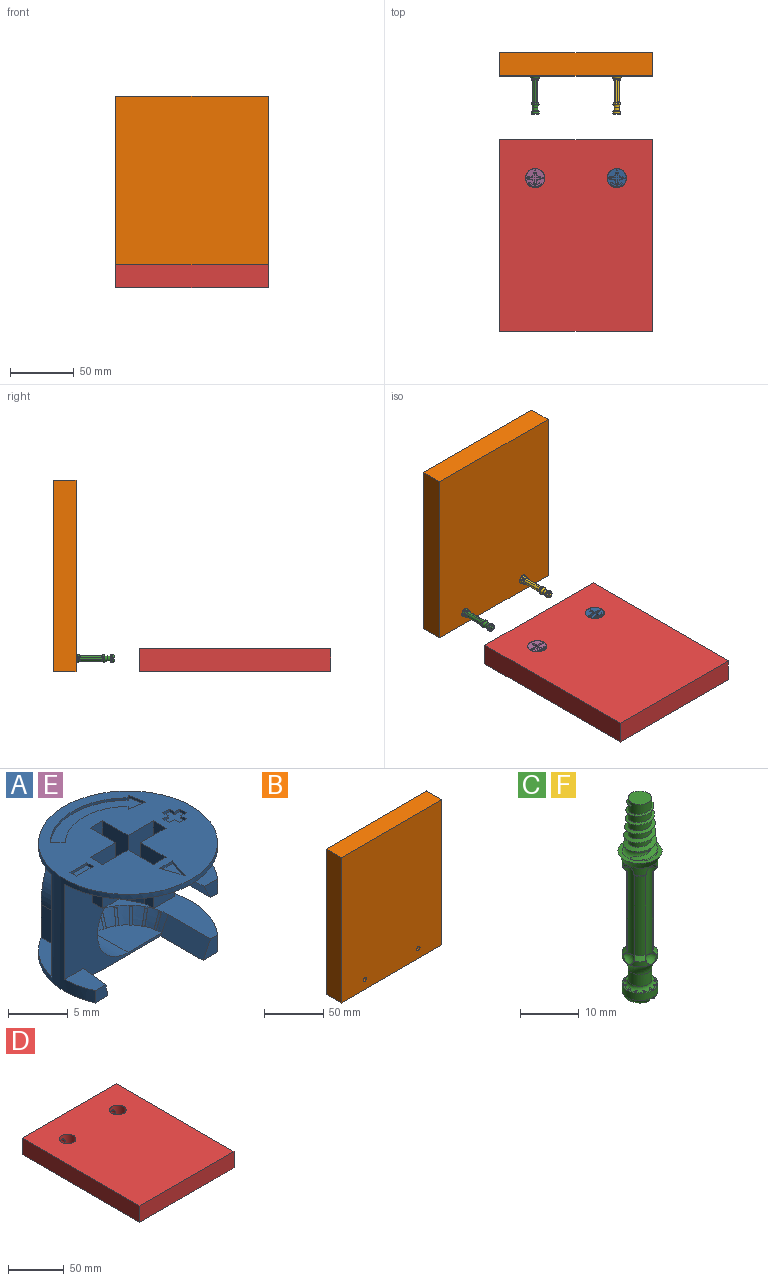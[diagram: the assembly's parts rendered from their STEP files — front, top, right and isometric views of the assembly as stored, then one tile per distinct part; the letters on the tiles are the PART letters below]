
ASSEMBLY  parts=6 mates=5
PART A: 154 faces, bbox 15x15x11.5 mm
  f0: plane 2.25x1.5mm, normal (0,1,0), area 3.4mm2, adj f1,f2,f22,f23
  f1: plane 15x15mm, normal (0,0,1), area 137.8mm2, adj f0,f2,f3,f15,f16,f17,f18,f19
  f2: plane 3x3mm, normal (-1,0,0), area 8.7mm2, adj f0,f1,f23,f24,f26
  f3: plane 2.25x1.5mm, normal (-1,0,0), area 3.4mm2, adj f1,f15,f24,f25
  f4: plane 3.25x2mm, normal (0.89,0.45,0), area 7.3mm2, adj f14,f31,f44,f49
  f5: plane 3.5x2mm, normal (-0.89,-0.45,0), area 7.8mm2, adj f9,f13,f32,f41
  f6: plane 3.5x2mm, normal (0.89,-0.45,0), area 7.8mm2, adj f7,f12,f32,f41
  f7: plane 3.5x1mm, normal (1,0,0), area 3.5mm2, adj f6,f8,f32,f41
  f8: plane 3.5x2.5mm, normal (0,-1,0), area 8.8mm2, adj f7,f13,f32,f41
  f9: plane 3.5x2mm, normal (0,-1,0), area 7mm2, adj f5,f32,f34,f41
  f10: plane 3.5x2mm, normal (0,1,0), area 7mm2, adj f33,f35,f57,f58
  f11: plane 3.46x1mm, normal (-1,0,0), area 3.5mm2, adj f29,f33,f58,f67
  f12: plane 3.5x2mm, normal (0,-1,0), area 7mm2, adj f6,f32,f36,f41,f62
  f13: plane 3.5x1mm, normal (-1,0,0), area 3.5mm2, adj f5,f8,f32,f41
  f14: plane 3.25x1mm, normal (1,0,0), area 3.3mm2, adj f4,f30,f31,f49
  f15: plane 3x3mm, normal (0,-1,0), area 8.7mm2, adj f1,f3,f25,f26,f27
  f16: plane 2.25x1.5mm, normal (0,-1,0), area 3.4mm2, adj f1,f17,f27,f28
  f17: plane 3x3mm, normal (1,0,0), area 8.7mm2, adj f1,f16,f18,f26,f28
  f18: plane 3x3mm, normal (0,-1,0), area 8.7mm2, adj f1,f17,f19,f21,f26
  f19: plane 2.25x1.5mm, normal (1,0,0), area 3.4mm2, adj f1,f18,f20,f21
  f20: plane 3x3mm, normal (0,1,0), area 8.7mm2, adj f1,f19,f21,f22,f26
  f21: plane 1.5x0.75mm, normal (0.71,0,0.71), area 1.6mm2, adj f18,f19,f20,f26
  f22: plane 3x3mm, normal (1,0,0), area 8.7mm2, adj f0,f1,f20,f23,f26
  f23: plane 1.5x0.75mm, normal (0,0.71,0.71), area 1.6mm2, adj f0,f2,f22,f26
  f24: plane 3x3mm, normal (0,1,0), area 8.7mm2, adj f1,f2,f3,f25,f26
  f25: plane 1.5x0.75mm, normal (-0.71,0,0.71), area 1.6mm2, adj f3,f15,f24,f26
  f26: plane 6x6mm, normal (0,0,1), area 15.8mm2, adj f2,f15,f17,f18,f20,f21,f22,f23
  f27: plane 3x3mm, normal (-1,0,0), area 8.7mm2, adj f1,f15,f16,f26,f28
  f28: plane 1.5x0.75mm, normal (0,-0.71,0.71), area 1.6mm2, adj f16,f17,f26,f27
  f29: plane 3.46x0.88mm, normal (0,1,0), area 2.9mm2, adj f11,f33,f53,f67
  f30: plane 3.25x0.88mm, normal (0,1,0), area 2.8mm2, adj f14,f31,f37,f49
  f31: plane 6.99x6.92mm, normal (0,0,-1), area 30.6mm2, adj f4,f14,f30,f37,f44,f45,f46,f47
  f32: plane 15x7.5mm, normal (0,0,-1), area 68.2mm2, adj f5,f6,f7,f8,f9,f12,f13,f34
  f33: plane 6.99x6.92mm, normal (0,0,-1), area 30.6mm2, adj f10,f11,f29,f35,f38,f39,f53,f56
  f34: plane 3.5x1.25mm, normal (-1,0,0), area 4.4mm2, adj f9,f32,f41,f51
  f35: plane 3.5x0.75mm, normal (-1,0,0), area 2.6mm2, adj f10,f33,f56,f57
  f36: plane 3.5x1.25mm, normal (1,0,0), area 4.4mm2, adj f12,f32,f40,f62
  f37: plane 3.25x3.24mm, normal (1,0,0), area 10.5mm2, adj f30,f31,f49,f69
  f38: plane 10.5x1.25mm, normal (0.88,0.47,0), area 14.9mm2, adj f33,f39,f55,f56
  f39: plane 10.5x0.13mm, normal (0,1,0), area 1.3mm2, adj f33,f38,f55,f69
  f40: plane 3.5x3.25mm, normal (0,-1,0), area 11.4mm2, adj f32,f36,f62,f69
  f41: plane 8.25x8.25mm, normal (0,0,-1), area 32.3mm2, adj f5,f6,f7,f8,f9,f12,f13,f34
  f42: plane 5x1.5mm, normal (-0.89,0,-0.45), area 8.4mm2, adj f41,f54,f62,f65,f149
  f43: plane 12.5x7.5mm, normal (0,0,1), area 37.2mm2, adj f50,f52,f64,f69,f70,f112
  f44: plane 3.25x2mm, normal (0,1,0), area 6.5mm2, adj f4,f31,f45,f49
  f45: plane 3.25x0.75mm, normal (1,0,0), area 2.4mm2, adj f31,f44,f46,f49
  f46: plane 3.25x2.25mm, normal (0,1,0), area 7.3mm2, adj f31,f45,f47,f49
  f47: plane 3.25x1.25mm, normal (-0.88,0.47,0), area 4.6mm2, adj f31,f46,f48,f49
  f48: plane 3.25x0.13mm, normal (0,1,0), area 0.4mm2, adj f31,f47,f49,f69
  f49: plane 6.99x6.92mm, normal (0,0,1), area 30.6mm2, adj f4,f14,f30,f37,f44,f45,f46,f47
  f50: cylinder r=2.12mm len=4.25mm, axis (0,1,0), area 18.4mm2, adj f43,f54,f69,f80
  f51: plane 11.5x11mm, normal (0,-1,0), area 45mm2, adj f32,f34,f41,f52,f60,f61,f63,f69
  f52: plane 5x1.75mm, normal (-0.89,0,0.45), area 9.8mm2, adj f43,f51,f63,f64,f112
  f53: plane 3.27x3.24mm, normal (-1,0,0), area 10.6mm2, adj f29,f33,f67,f69
  f54: plane 12.5x7.5mm, normal (0,0,-1), area 37.2mm2, adj f42,f50,f65,f68,f69,f149
  f55: plane 5.92x3.42mm, normal (0,0,1), area 13.9mm2, adj f38,f39,f56,f66,f69
  f56: plane 10.5x5.13mm, normal (0,1,0), area 28.7mm2, adj f33,f35,f38,f55,f57,f66,f67
  f57: plane 2.88x2.51mm, normal (0,0,-1), area 2.9mm2, adj f10,f35,f56,f58,f67
  f58: plane 3.5x2mm, normal (-0.89,0.45,0), area 7.8mm2, adj f10,f11,f33,f57,f67
  f59: plane 1.5x1.25mm, normal (0,-1,0), area 1.7mm2, adj f60,f61,f63,f69
  f60: plane 3x2.25mm, normal (0,0,1), area 5.6mm2, adj f51,f59,f61,f69
  f61: plane 3x1.25mm, normal (0.97,-0.12,0.2), area 3.9mm2, adj f51,f59,f60,f63
  f62: plane 5x3.5mm, normal (0,0,1), area 14.2mm2, adj f12,f36,f40,f42,f65,f68
  f63: plane 15x12.5mm, normal (0,0,-1), area 109.8mm2, adj f51,f52,f59,f61,f64,f69,f70
  f64: plane 1.75x1.72mm, normal (0,-1,0), area 2.2mm2, adj f43,f52,f63,f70
  f65: plane 1.59x1.5mm, normal (0,-1,0), area 1.8mm2, adj f42,f54,f62,f68
  f66: plane 5.92x3.38mm, normal (-1,0,0), area 20mm2, adj f55,f56,f67,f69
  f67: cylinder r=3.88mm len=6.99mm, axis (0,-1,0), area 33.2mm2, adj f11,f29,f53,f56,f57,f58,f66,f69
  f68: cylinder r=7.5mm len=5mm, axis (0,0,-1), area 8.2mm2, adj f54,f62,f65,f69
  f69: cylinder r=7.5mm len=15mm, axis (0,0,-1), area 120.2mm2, adj f1,f31,f32,f33,f37,f39,f40,f43
  f70: cylinder r=7.5mm len=5mm, axis (0,0,-1), area 9.6mm2, adj f43,f63,f64,f69
  f71: plane 2.25x1.5mm, normal (0,0,1), area 1.7mm2, adj f72,f73,f74
  f72: plane 2.25x0.75mm, normal (0.95,0.32,0), area 0.6mm2, adj f1,f71,f73,f74
  f73: plane 1.5x0.25mm, normal (0,-1,0), area 0.4mm2, adj f1,f71,f72,f74
  f74: plane 2.25x0.75mm, normal (-0.95,0.32,0), area 0.6mm2, adj f1,f71,f72,f73
  f75: cylinder r=3.62mm len=7.25mm, axis (0,1,0), area 45.5mm2, adj f41,f51,f76,f77,f80,f82,f83,f111
  f76: plane 1.41x0.71mm, normal (0,-0.89,0.45), area 0.4mm2, adj f75,f77,f78,f79,f111
  f77: plane 1.42x0.76mm, normal (-1,0,0), area 0.1mm2, adj f75,f76,f78,f80
  f78: plane 0.25x0.05mm, normal (0,0.45,0.89), area 0mm2, adj f76,f77,f79,f80,f112
  f79: plane 1.41x0.75mm, normal (1,0,0), area 0.1mm2, adj f76,f78,f111,f112
  f80: cone r=2.88mm half-angle=63.4deg, axis (0,-1,0), area 14.7mm2, adj f50,f75,f77,f78,f81,f82,f112,f149
  f81: plane 0.25x0.05mm, normal (0,0.45,-0.89), area 0mm2, adj f80,f82,f83,f84,f149
  f82: plane 1.42x0.76mm, normal (-1,0,0), area 0.1mm2, adj f75,f80,f81,f83
  f83: plane 1.41x0.71mm, normal (0,-0.89,-0.45), area 0.4mm2, adj f41,f75,f81,f82,f84
  f84: plane 1.41x0.75mm, normal (1,0,0), area 0.1mm2, adj f41,f81,f83,f149
  f85: plane 0.75x0.25mm, normal (0,-1,0), area 0.2mm2, adj f1,f89,f90,f91
  f86: plane 0.63x0.25mm, normal (-1,0,0), area 0.2mm2, adj f1,f87,f91,f97
  f87: plane 0.75x0.25mm, normal (0,1,0), area 0.2mm2, adj f1,f86,f88,f91
  f88: plane 0.63x0.25mm, normal (1,0,0), area 0.2mm2, adj f1,f87,f91,f96
  f89: plane 0.63x0.25mm, normal (-1,0,0), area 0.2mm2, adj f1,f85,f91,f95
  f90: plane 0.63x0.25mm, normal (1,0,0), area 0.2mm2, adj f1,f85,f91,f92
  f91: plane 2x2mm, normal (0,0,1), area 2.4mm2, adj f85,f86,f87,f88,f89,f90,f92,f93
  f92: plane 0.63x0.25mm, normal (0,-1,0), area 0.2mm2, adj f1,f90,f91,f94
  f93: plane 0.75x0.25mm, normal (-1,0,0), area 0.2mm2, adj f1,f91,f95,f97
  f94: plane 0.75x0.25mm, normal (1,0,0), area 0.2mm2, adj f1,f91,f92,f96
  f95: plane 0.63x0.25mm, normal (0,-1,0), area 0.2mm2, adj f1,f89,f91,f93
  f96: plane 0.63x0.25mm, normal (0,1,0), area 0.2mm2, adj f1,f88,f91,f94
  f97: plane 0.63x0.25mm, normal (0,1,0), area 0.2mm2, adj f1,f86,f91,f93
  f98: plane 2x0.75mm, normal (0,0,1), area 1.5mm2, adj f99,f100,f101,f102
  f99: plane 2x0.25mm, normal (0,-1,0), area 0.5mm2, adj f1,f98,f100,f102
  f100: plane 0.75x0.25mm, normal (-1,0,0), area 0.2mm2, adj f1,f98,f99,f101
  f101: plane 2x0.25mm, normal (0,1,0), area 0.5mm2, adj f1,f98,f100,f102
  f102: plane 0.75x0.25mm, normal (1,0,0), area 0.2mm2, adj f1,f98,f99,f101
  f103: plane 9.81x3.41mm, normal (0,0,1), area 13mm2, adj f104,f105,f106,f107,f108,f109,f110
  f104: plane 1.77x0.35mm, normal (-0.98,-0.2,0), area 0.5mm2, adj f1,f103,f105,f110
  f105: plane 1.77x0.35mm, normal (0.2,0.98,0), area 0.5mm2, adj f1,f103,f104,f106
  f106: plane 0.27x0.27mm, normal (0.71,-0.71,0), area 0.1mm2, adj f1,f103,f105,f107
  f107: cylinder r=5.25mm len=7.42mm, axis (0,0,-1), area 2.1mm2, adj f1,f103,f106,f108
  f108: plane 0.88x0.88mm, normal (0.71,0.71,0), area 0.3mm2, adj f1,f103,f107,f109
  f109: cylinder r=6.5mm len=9.19mm, axis (0,0,1), area 2.6mm2, adj f1,f103,f108,f110
  f110: plane 0.27x0.27mm, normal (0.71,-0.71,0), area 0.1mm2, adj f1,f103,f104,f109
  f111: plane 4x4mm, normal (0,0,1), area 12.5mm2, adj f51,f75,f76,f79,f112,f113,f114,f115
  f112: cone r=4.38mm half-angle=26.6deg, axis (0,0,1), area 9.4mm2, adj f43,f52,f78,f79,f80,f111,f114,f115
  f113: plane 1.41x0.75mm, normal (-0.25,-0.86,0.45), area 0.4mm2, adj f111,f114,f115,f116
  f114: plane 1.41x0.72mm, normal (0.96,-0.28,0), area 0.1mm2, adj f111,f112,f113,f116
  f115: plane 1.41x0.72mm, normal (-0.96,0.28,0), area 0.1mm2, adj f111,f112,f113,f116
  f116: plane 0.25x0.11mm, normal (0.12,0.43,0.89), area 0mm2, adj f112,f113,f114,f115
  f117: plane 1.41x0.73mm, normal (-0.47,-0.76,0.45), area 0.4mm2, adj f111,f118,f119,f120
  f118: plane 1.41x0.64mm, normal (0.85,-0.53,0), area 0.1mm2, adj f111,f112,f117,f120
  f119: plane 1.41x0.64mm, normal (-0.85,0.53,0), area 0.1mm2, adj f111,f112,f117,f120
  f120: plane 0.24x0.17mm, normal (0.24,0.38,0.89), area 0mm2, adj f112,f117,f118,f119
  f121: plane 1.41x0.69mm, normal (-0.66,-0.6,0.45), area 0.4mm2, adj f111,f122,f123,f124
  f122: plane 1.41x0.56mm, normal (0.67,-0.74,0), area 0.1mm2, adj f111,f112,f121,f124
  f123: plane 1.41x0.56mm, normal (-0.67,0.74,0), area 0.1mm2, adj f111,f112,f121,f124
  f124: plane 0.22x0.2mm, normal (0.33,0.3,0.89), area 0mm2, adj f112,f121,f122,f123
  f125: plane 1.41x0.74mm, normal (-0.8,-0.39,0.45), area 0.4mm2, adj f111,f126,f127,f128
  f126: plane 1.41x0.67mm, normal (0.44,-0.9,0), area 0.1mm2, adj f111,f112,f125,f128
  f127: plane 1.41x0.67mm, normal (-0.44,0.9,0), area 0.1mm2, adj f111,f112,f125,f128
  f128: plane 0.25x0.15mm, normal (0.4,0.2,0.89), area 0mm2, adj f112,f125,f126,f127
  f129: plane 1.41x0.74mm, normal (-0.88,-0.16,0.45), area 0.4mm2, adj f111,f130,f131,f132
  f130: plane 1.41x0.74mm, normal (0.17,-0.98,0), area 0.1mm2, adj f111,f112,f129,f132
  f131: plane 1.41x0.74mm, normal (-0.17,0.98,0), area 0.1mm2, adj f111,f112,f129,f132
  f132: plane 0.26x0.09mm, normal (0.44,0.08,0.89), area 0mm2, adj f112,f129,f130,f131
  f133: plane 0.25x0.11mm, normal (0.12,0.43,-0.89), area 0mm2, adj f134,f135,f136,f149
  f134: plane 1.41x0.72mm, normal (0.96,-0.28,0), area 0.1mm2, adj f41,f133,f136,f149
  f135: plane 1.41x0.72mm, normal (-0.96,0.28,0), area 0.1mm2, adj f41,f133,f136,f149
  f136: plane 1.41x0.75mm, normal (-0.25,-0.86,-0.45), area 0.4mm2, adj f41,f133,f134,f135
  f137: plane 0.24x0.17mm, normal (0.24,0.38,-0.89), area 0mm2, adj f138,f139,f140,f149
  f138: plane 1.41x0.64mm, normal (0.85,-0.53,0), area 0.1mm2, adj f41,f137,f140,f149
  f139: plane 1.41x0.64mm, normal (-0.85,0.53,0), area 0.1mm2, adj f41,f137,f140,f149
  f140: plane 1.41x0.73mm, normal (-0.47,-0.76,-0.45), area 0.4mm2, adj f41,f137,f138,f139
  f141: plane 0.22x0.2mm, normal (0.33,0.3,-0.89), area 0mm2, adj f142,f143,f144,f149
  f142: plane 1.41x0.56mm, normal (0.67,-0.74,0), area 0.1mm2, adj f41,f141,f144,f149
  f143: plane 1.41x0.56mm, normal (-0.67,0.74,0), area 0.1mm2, adj f41,f141,f144,f149
  f144: plane 1.41x0.69mm, normal (-0.66,-0.6,-0.45), area 0.4mm2, adj f41,f141,f142,f143
  f145: plane 0.25x0.15mm, normal (0.4,0.2,-0.89), area 0mm2, adj f146,f147,f148,f149
  f146: plane 1.41x0.67mm, normal (0.44,-0.9,0), area 0.1mm2, adj f41,f145,f148,f149
  f147: plane 1.41x0.67mm, normal (-0.44,0.9,0), area 0.1mm2, adj f41,f145,f148,f149
  f148: plane 1.41x0.74mm, normal (-0.8,-0.39,-0.45), area 0.4mm2, adj f41,f145,f146,f147
  f149: cone r=4.75mm half-angle=26.6deg, axis (0,0,-1), area 9.4mm2, adj f41,f42,f54,f80,f81,f84,f133,f134
  f150: plane 0.26x0.09mm, normal (0.44,0.08,-0.89), area 0mm2, adj f149,f151,f152,f153
  f151: plane 1.41x0.74mm, normal (0.17,-0.98,0), area 0.1mm2, adj f41,f149,f150,f153
  f152: plane 1.41x0.74mm, normal (-0.17,0.98,0), area 0.1mm2, adj f41,f149,f150,f153
  f153: plane 1.41x0.74mm, normal (-0.88,-0.16,-0.45), area 0.4mm2, adj f41,f150,f151,f152
PART B: 10 faces, bbox 120x18x150 mm
  f0: plane 150x18mm, normal (-1,0,0), area 2700mm2, adj f1,f3,f4,f5
  f1: plane 120x18mm, normal (0,0,-1), area 2160mm2, adj f0,f2,f4,f5
  f2: plane 150x18mm, normal (1,0,0), area 2700mm2, adj f1,f3,f4,f5
  f3: plane 120x18mm, normal (0,0,1), area 2160mm2, adj f0,f2,f4,f5
  f4: plane 150x120mm, normal (0,-1,0), area 17974.9mm2, adj f0,f1,f2,f3,f6,f8
  f5: plane 150x120mm, normal (0,1,0), area 18000mm2, adj f0,f1,f2,f3
  f6: cylinder r=2mm len=11mm, axis (0,-1,0), area 138.2mm2, adj f4,f7
  f7: plane 4x4mm, normal (0,-1,0), area 12.6mm2, adj f6
  f8: cylinder r=2mm len=11mm, axis (0,-1,0), area 138.2mm2, adj f4,f9
  f9: plane 4x4mm, normal (0,-1,0), area 12.6mm2, adj f8
PART C: 132 faces, bbox 8.2x8.2x41.2 mm
  f0: plane 2.21x2.07mm, normal (0,-1,-0.09), area 3.9mm2, adj f1,f6,f8,f9,f17
  f1: plane 2.52x2.17mm, normal (1,0,-0.09), area 3.8mm2, adj f0,f6,f8,f16,f17,f20
  f2: plane 2.52x2.17mm, normal (-1,0,-0.09), area 3.8mm2, adj f3,f6,f13,f16,f19,f20
  f3: plane 2.21x2.07mm, normal (0,-1,-0.09), area 3.9mm2, adj f2,f6,f12,f13,f19
  f4: plane 2.52x2.17mm, normal (1,0,-0.09), area 3.8mm2, adj f5,f6,f10,f11,f17,f18
  f5: plane 2.21x2.07mm, normal (0,1,-0.09), area 3.9mm2, adj f4,f6,f9,f10,f17
  f6: plane 5.15x4.83mm, normal (0,0,-1), area 10.1mm2, adj f0,f1,f2,f3,f4,f5,f7,f9
  f7: plane 2.21x2.07mm, normal (0,1,-0.09), area 3.9mm2, adj f6,f12,f14,f15,f19
  f8: plane 1.1x1.1mm, normal (0,0,-1), area 0.8mm2, adj f0,f1,f17
  f9: plane 1.69x1.43mm, normal (1,0,-0.09), area 2.2mm2, adj f0,f5,f6,f17
  f10: plane 1.1x1.1mm, normal (0,0,-1), area 0.8mm2, adj f4,f5,f17
  f11: plane 1.33x1mm, normal (0,1,-0.09), area 1.2mm2, adj f4,f6,f14,f18
  f12: plane 1.69x1.43mm, normal (-1,0,-0.09), area 2.2mm2, adj f3,f6,f7,f19
  f13: plane 1.1x1.1mm, normal (0,0,-1), area 0.8mm2, adj f2,f3,f19
  f14: plane 2.52x2.17mm, normal (-1,0,-0.09), area 3.8mm2, adj f6,f7,f11,f15,f18,f19
  f15: plane 1.1x1.1mm, normal (0,0,-1), area 0.8mm2, adj f7,f14,f19
  f16: plane 1.33x1mm, normal (0,-1,-0.09), area 1.2mm2, adj f1,f2,f6,f20
  f17: torus R=2mm, axis (0,0,1), area 9.2mm2, adj f0,f1,f4,f5,f8,f9,f10,f32
  f18: plane 1.33x0.5mm, normal (0,0,-1), area 0.6mm2, adj f4,f11,f14,f32
  f19: torus R=2mm, axis (0,0,1), area 9.2mm2, adj f2,f3,f7,f12,f13,f14,f15,f32
  f20: plane 1.33x0.5mm, normal (0,0,-1), area 0.6mm2, adj f1,f2,f16,f32
  f21: torus R=2.88mm, axis (0,0,1), area 0mm2, adj f32,f36,f37,f38
  f22: torus R=2.88mm, axis (0,0,1), area 0mm2, adj f32,f40,f41,f42
  f23: torus R=2.88mm, axis (0,0,1), area 0mm2, adj f32,f44,f45,f46
  f24: torus R=2.88mm, axis (0,0,1), area 0mm2, adj f32,f48,f49,f50
  f25: torus R=2.88mm, axis (0,0,1), area 0mm2, adj f32,f52,f53,f54
  f26: torus R=2.88mm, axis (0,0,1), area 0mm2, adj f32,f56,f57,f58
  f27: torus R=2.88mm, axis (0,0,1), area 0mm2, adj f32,f60,f61,f62
  f28: torus R=2.88mm, axis (0,0,1), area 0mm2, adj f32,f64,f65,f66
  f29: torus R=2.88mm, axis (0,0,1), area 0mm2, adj f32,f68,f69,f70
  f30: torus R=2.88mm, axis (0,0,1), area 0mm2, adj f32,f72,f73,f74
  f31: torus R=2.88mm, axis (0,0,1), area 0mm2, adj f32,f76,f77,f78
  f32: cylinder r=3mm len=6mm, axis (0,0,-1), area 28.3mm2, adj f17,f18,f19,f20,f21,f22,f23,f24
  f33: torus R=2.88mm, axis (0,0,1), area 0mm2, adj f32,f34,f80,f81
  f34: plane 0.58x0.34mm, normal (-0.87,0.5,0), area 0.1mm2, adj f33,f35,f81,f82
  f35: plane 1.27x0.56mm, normal (0,0,1), area 0.3mm2, adj f32,f34,f36,f82
  f36: plane 0.67x0.13mm, normal (1,0,0), area 0.1mm2, adj f21,f35,f37,f82
  f37: plane 0.54x0.25mm, normal (0,0,1), area 0.1mm2, adj f21,f36,f38,f82
  f38: plane 0.67x0.13mm, normal (-1,0,0), area 0.1mm2, adj f21,f37,f39,f82
  f39: plane 1.27x0.56mm, normal (0,0,1), area 0.3mm2, adj f32,f38,f40,f82
  f40: plane 0.58x0.34mm, normal (0.87,0.5,0), area 0.1mm2, adj f22,f39,f41,f82
  f41: plane 0.59x0.49mm, normal (0,0,1), area 0.1mm2, adj f22,f40,f42,f82
  f42: plane 0.58x0.34mm, normal (-0.87,-0.5,0), area 0.1mm2, adj f22,f41,f43,f82
  f43: plane 1.05x1.05mm, normal (0,0,1), area 0.3mm2, adj f32,f42,f44,f82
  f44: plane 0.58x0.34mm, normal (0.5,0.87,0), area 0.1mm2, adj f23,f43,f45,f82
  f45: plane 0.59x0.49mm, normal (0,0,1), area 0.1mm2, adj f23,f44,f46,f82
  f46: plane 0.58x0.34mm, normal (-0.5,-0.87,0), area 0.1mm2, adj f23,f45,f47,f82
  f47: plane 1.27x0.56mm, normal (0,0,1), area 0.3mm2, adj f32,f46,f48,f82
  f48: plane 0.67x0.13mm, normal (0,1,0), area 0.1mm2, adj f24,f47,f49,f82
  f49: plane 0.54x0.25mm, normal (0,0,1), area 0.1mm2, adj f24,f48,f50,f82
  f50: plane 0.67x0.13mm, normal (0,-1,0), area 0.1mm2, adj f24,f49,f51,f82
  f51: plane 1.27x0.56mm, normal (0,0,1), area 0.3mm2, adj f32,f50,f52,f82
  f52: plane 0.58x0.34mm, normal (-0.5,0.87,0), area 0.1mm2, adj f25,f51,f53,f82
  f53: plane 0.59x0.49mm, normal (0,0,1), area 0.1mm2, adj f25,f52,f54,f82
  f54: plane 0.58x0.34mm, normal (0.5,-0.87,0), area 0.1mm2, adj f25,f53,f55,f82
  f55: plane 1.05x1.05mm, normal (0,0,1), area 0.3mm2, adj f32,f54,f56,f82
  f56: plane 0.58x0.34mm, normal (-0.87,0.5,0), area 0.1mm2, adj f26,f55,f57,f82
  f57: plane 0.59x0.49mm, normal (0,0,1), area 0.1mm2, adj f26,f56,f58,f82
  f58: plane 0.58x0.34mm, normal (0.87,-0.5,0), area 0.1mm2, adj f26,f57,f59,f82
  f59: plane 1.27x0.56mm, normal (0,0,1), area 0.3mm2, adj f32,f58,f60,f82
  f60: plane 0.67x0.13mm, normal (-1,0,0), area 0.1mm2, adj f27,f59,f61,f82
  f61: plane 0.54x0.25mm, normal (0,0,1), area 0.1mm2, adj f27,f60,f62,f82
  f62: plane 0.67x0.13mm, normal (1,0,0), area 0.1mm2, adj f27,f61,f63,f82
  f63: plane 1.27x0.56mm, normal (0,0,1), area 0.3mm2, adj f32,f62,f64,f82
  f64: plane 0.58x0.34mm, normal (-0.87,-0.5,0), area 0.1mm2, adj f28,f63,f65,f82
  f65: plane 0.59x0.49mm, normal (0,0,1), area 0.1mm2, adj f28,f64,f66,f82
  f66: plane 0.58x0.34mm, normal (0.87,0.5,0), area 0.1mm2, adj f28,f65,f67,f82
  f67: plane 1.05x1.05mm, normal (0,0,1), area 0.3mm2, adj f32,f66,f68,f82
  f68: plane 0.58x0.34mm, normal (-0.5,-0.87,0), area 0.1mm2, adj f29,f67,f69,f82
  f69: plane 0.59x0.49mm, normal (0,0,1), area 0.1mm2, adj f29,f68,f70,f82
  f70: plane 0.58x0.34mm, normal (0.5,0.87,0), area 0.1mm2, adj f29,f69,f71,f82
  f71: plane 1.27x0.56mm, normal (0,0,1), area 0.3mm2, adj f32,f70,f72,f82
  f72: plane 0.67x0.13mm, normal (0,-1,0), area 0.1mm2, adj f30,f71,f73,f82
  f73: plane 0.54x0.25mm, normal (0,0,1), area 0.1mm2, adj f30,f72,f74,f82
  f74: plane 0.67x0.13mm, normal (0,1,0), area 0.1mm2, adj f30,f73,f75,f82
  f75: plane 1.27x0.56mm, normal (0,0,1), area 0.3mm2, adj f32,f74,f76,f82
  f76: plane 0.58x0.34mm, normal (0.5,-0.87,0), area 0.1mm2, adj f31,f75,f77,f82
  f77: plane 0.59x0.49mm, normal (0,0,1), area 0.1mm2, adj f31,f76,f78,f82
  f78: plane 0.58x0.34mm, normal (-0.5,0.87,0), area 0.1mm2, adj f31,f77,f79,f82
  f79: plane 1.05x1.05mm, normal (0,0,1), area 0.3mm2, adj f32,f78,f80,f82
  f80: plane 0.58x0.34mm, normal (0.87,-0.5,0), area 0.1mm2, adj f33,f79,f81,f82
  f81: plane 0.59x0.49mm, normal (0,0,1), area 0.1mm2, adj f33,f34,f80,f82
  f82: torus R=2.75mm, axis (0,0,1), area 15.5mm2, adj f34,f35,f36,f37,f38,f39,f40,f41
  f83: cylinder r=2mm len=4mm, axis (0,0,-1), area 30.2mm2, adj f82,f84
  f84: torus R=5.25mm, axis (0,0,1), area 37.3mm2, adj f83,f85
  f85: cone r=3mm half-angle=45deg, axis (0,0,1), area 1.3mm2, adj f84,f86,f87,f88,f89
  f86: cylinder r=3mm len=3mm, axis (0,0,-1), area 3.5mm2, adj f85,f91,f92,f93
  f87: cylinder r=3mm len=3mm, axis (0,0,-1), area 3.5mm2, adj f85,f90,f91,f95
  f88: cylinder r=3mm len=3mm, axis (0,0,-1), area 3.5mm2, adj f85,f93,f94,f96
  f89: cylinder r=3mm len=3mm, axis (0,0,-1), area 3.5mm2, adj f85,f95,f96,f97
  f90: cone r=2.25mm half-angle=45deg, axis (0,0,-1), area 2mm2, adj f87,f91,f95,f98,f99,f103
  f91: sphere r=1.25mm, area 4.3mm2, adj f86,f87,f90,f92,f99
  f92: cone r=2.25mm half-angle=45deg, axis (0,0,-1), area 2mm2, adj f86,f91,f93,f99,f100,f101
  f93: sphere r=1.25mm, area 4.3mm2, adj f86,f88,f92,f94,f101
  f94: cone r=2.25mm half-angle=45deg, axis (0,0,-1), area 2mm2, adj f88,f93,f96,f101,f102,f104
  f95: sphere r=1.25mm, area 4.4mm2, adj f87,f89,f90,f97,f103
  f96: sphere r=1.25mm, area 4.3mm2, adj f88,f89,f94,f97,f104
  f97: cone r=2.25mm half-angle=45deg, axis (0,0,-1), area 2mm2, adj f89,f95,f96,f103,f104,f105
  f98: cylinder r=2.25mm len=16.5mm, axis (0,0,-1), area 29.6mm2, adj f90,f99,f103,f106
  f99: cylinder r=1.25mm len=18mm, axis (0,0,-1), area 34.9mm2, adj f90,f91,f92,f98,f100,f106,f107,f108
  f100: cylinder r=2.25mm len=16.5mm, axis (0,0,-1), area 29.6mm2, adj f92,f99,f101,f108
  f101: cylinder r=1.25mm len=18mm, axis (0,0,-1), area 34.9mm2, adj f92,f93,f94,f100,f102,f108,f109,f110
  f102: cylinder r=2.25mm len=16.5mm, axis (0,0,-1), area 29.6mm2, adj f94,f101,f104,f110
  f103: cylinder r=1.25mm len=18mm, axis (0,0,-1), area 34.9mm2, adj f90,f95,f97,f98,f105,f106,f111,f113
  f104: cylinder r=1.25mm len=18mm, axis (0,0,-1), area 34.9mm2, adj f94,f96,f97,f102,f105,f110,f112,f113
  f105: cylinder r=2.25mm len=16.5mm, axis (0,0,-1), area 29.6mm2, adj f97,f103,f104,f113
  f106: cone r=3mm half-angle=45deg, axis (0,0,1), area 2mm2, adj f98,f99,f103,f114
  f107: sphere r=1.25mm, area 4.4mm2, adj f99,f114,f115
  f108: cone r=3mm half-angle=45deg, axis (0,0,1), area 2mm2, adj f99,f100,f101,f115
  f109: sphere r=1.25mm, area 4.4mm2, adj f101,f115,f116
  f110: cone r=3mm half-angle=45deg, axis (0,0,1), area 2mm2, adj f101,f102,f104,f116
  f111: sphere r=1.25mm, area 4.4mm2, adj f103,f114,f117
  f112: sphere r=1.25mm, area 4.4mm2, adj f104,f116,f117
  f113: cone r=3mm half-angle=45deg, axis (0,0,1), area 2mm2, adj f103,f104,f105,f117
  f114: cylinder r=3mm len=3mm, axis (0,0,-1), area 4mm2, adj f99,f103,f106,f107,f111,f118
  f115: cylinder r=3mm len=3mm, axis (0,0,-1), area 4mm2, adj f99,f101,f107,f108,f109,f118
  f116: cylinder r=3mm len=3mm, axis (0,0,-1), area 4mm2, adj f101,f104,f109,f110,f112,f118
  f117: cylinder r=3mm len=3mm, axis (0,0,-1), area 4mm2, adj f103,f104,f111,f112,f113,f118
  f118: cone r=3.75mm half-angle=26.6deg, axis (0,0,1), area 35.6mm2, adj f114,f115,f116,f117,f120
  f119: plane 4x4mm, normal (0,0,1), area 12.6mm2, adj f131
  f120: plane 7.5x7.5mm, normal (0,0,1), area 15.9mm2, adj f118,f123
  f121: plane 0.27x0.2mm, normal (0,-1,0), area 0mm2, adj f122,f125,f131
  f122: bspline ~10.74x5.67mm, area 55.8mm2, adj f121,f123,f125,f126,f127,f128,f129,f130
  f123: torus R=3mm, axis (0,0,1), area 17.2mm2, adj f120,f122,f124,f125,f126
  f124: torus R=3mm, axis (0,0,1), area 0.4mm2, adj f123,f125,f126
  f125: bspline ~10.83x6.79mm, area 59.1mm2, adj f121,f122,f123,f124,f126,f127,f128,f129
  f126: cylinder r=2mm len=4mm, axis (0,0,-1), area 8.6mm2, adj f122,f123,f124,f125,f127
  f127: cylinder r=2mm len=4mm, axis (0,0,-1), area 14.6mm2, adj f122,f125,f126,f128
  f128: cylinder r=2mm len=4mm, axis (0,0,-1), area 15.7mm2, adj f122,f125,f127,f129
  f129: cylinder r=2mm len=4mm, axis (0,0,-1), area 16.9mm2, adj f122,f125,f128,f130
  f130: cylinder r=2mm len=4mm, axis (0,0,-1), area 18mm2, adj f122,f125,f129,f131
  f131: cylinder r=2mm len=4mm, axis (0,0,-1), area 21.7mm2, adj f119,f121,f122,f125,f130
PART D: 12 faces, bbox 120x150x18 mm
  f0: plane 120x18mm, normal (0,1,0), area 2083mm2, adj f1,f3,f4,f5,f10,f11
  f1: plane 150x18mm, normal (-1,0,0), area 2700mm2, adj f0,f2,f4,f5
  f2: plane 120x18mm, normal (0,-1,0), area 2160mm2, adj f1,f3,f4,f5
  f3: plane 150x18mm, normal (1,0,0), area 2700mm2, adj f0,f2,f4,f5
  f4: plane 150x120mm, normal (0,0,1), area 17646.6mm2, adj f0,f1,f2,f3,f6,f8
  f5: plane 150x120mm, normal (0,0,-1), area 18000mm2, adj f0,f1,f2,f3
  f6: cylinder r=7.5mm len=15mm, axis (0,0,1), area 525.9mm2, adj f4,f7,f11
  f7: plane 15x15mm, normal (0,0,1), area 176.7mm2, adj f6
  f8: cylinder r=7.5mm len=15mm, axis (0,0,1), area 525.9mm2, adj f4,f9,f10
  f9: plane 15x15mm, normal (0,0,1), area 176.7mm2, adj f8
  f10: cylinder r=3.5mm len=23.37mm, axis (0,1,0), area 504.2mm2, adj f0,f8
  f11: cylinder r=3.5mm len=23.37mm, axis (0,1,0), area 504.2mm2, adj f0,f6
PART E: same geometry as A
PART F: same geometry as C
PLACE A rot(axis=(0,0,-1),180deg) t=(92,-80,18)mm
PLACE B t=(0,18,0)mm fixed
PLACE C rot(axis=(-1,0,0),90deg) t=(28,-30,10.37)mm
PLACE D t=(0,-50,0)mm
PLACE E rot(axis=(0,0,1),180deg) t=(28,-80,18)mm
PLACE F rot(axis=(-1,0,0),90deg) t=(92,-30,10.38)mm
MATE fastened F.f118 <-> B.f6  axis (0,1,0) through (92,0,10.38)mm
MATE slider D.f0 <-> B.f4  axis (0,1,0) through (60,-50,0)mm
MATE revolute A.f68 <-> D.f6  axis (0,0,1) through (92,-80,18)mm
MATE fastened C.f123 <-> B.f8  axis (0,1,0) through (28,0,10.37)mm
MATE revolute E.f68 <-> D.f8  axis (0,0,1) through (28,-80,18)mm
